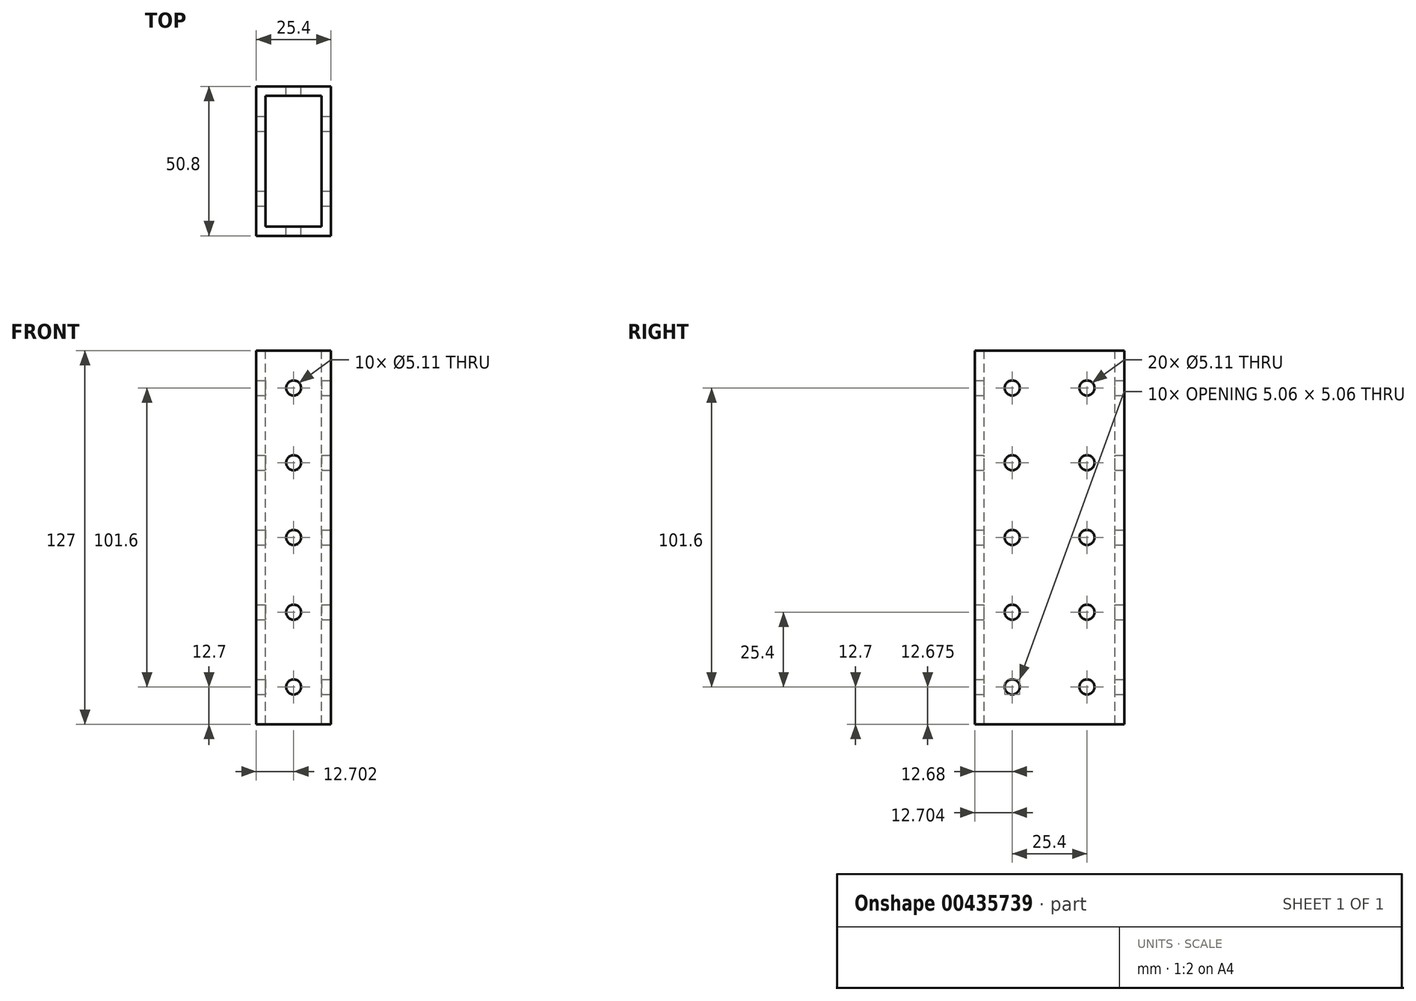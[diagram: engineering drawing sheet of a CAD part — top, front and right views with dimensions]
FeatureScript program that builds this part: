
annotation { "Feature Type Name" : "Feature", "Feature Type Description" : "" }
export const myFeature = defineFeature(function(context is Context, id is Id, definition is map)
    precondition{}
    {
        {
            var Q0;
            Q0=qCreatedBy(makeId("Top.planeOp"),FACE);
            var sketch = newSketch(context, id + "F0", { "sketchPlane" : qUnion([Q0])});
            skLineSegment(sketch, "E0.bottom", {"start": v(-9.87, 8.95) * mm, "end": v(15.53, 8.95) * mm});
            skLineSegment(sketch, "E0.top", {"start": v(-9.87, -41.85) * mm, "end": v(15.53, -41.85) * mm});
            skLineSegment(sketch, "E0.left", {"start": v(-9.87, 8.95) * mm, "end": v(-9.87, -41.85) * mm});
            skLineSegment(sketch, "E0.right", {"start": v(15.53, 8.95) * mm, "end": v(15.53, -41.85) * mm});
            skSolve(sketch);
        }
        {
            var Q0;
            Q0=makeQuery(id+"F0.imprint","IMPRINT",FACE,{"disambiguationData":[TD([[makeQuery(id+"F0.imprint","IMPRINT",EDGE,{"derivedFrom":sQuery(id+"F0.wireOp",EDGE,"E0.bottom")}),-1.0]])]});
            extrude(context, id + "F1", {"entities" : qUnion([Q0]), "depth" : 127 * mm});
        }
        {
            var Q0;
            Q0=makeQuery(id+"F1.opExtrude","CAP_FACE",FACE,{"disambiguationData":[OSD([sQuery(id+"F0.wireOp",EDGE,"E0.bottom"),sQuery(id+"F0.wireOp",EDGE,"E0.top"),sQuery(id+"F0.wireOp",EDGE,"E0.left"),sQuery(id+"F0.wireOp",EDGE,"E0.right")])],"isStart":false});
            var sketch = newSketch(context, id + "F2", { "sketchPlane" : qUnion([Q0])});
            skLineSegment(sketch, "E1.bottom", {"start": v(-6.7, 5.78) * mm, "end": v(12.36, 5.78) * mm});
            skLineSegment(sketch, "E1.top", {"start": v(-6.7, -38.67) * mm, "end": v(12.36, -38.67) * mm});
            skLineSegment(sketch, "E1.left", {"start": v(-6.7, 5.78) * mm, "end": v(-6.7, -38.67) * mm});
            skLineSegment(sketch, "E1.right", {"start": v(12.36, 5.78) * mm, "end": v(12.36, -38.67) * mm});
            skSolve(sketch);
        }
        {
            var Q0;
            Q0=makeQuery(id+"F2.imprint","IMPRINT",FACE,{"disambiguationData":[TD([[makeQuery(id+"F2.imprint","IMPRINT",EDGE,{"derivedFrom":sQuery(id+"F2.wireOp",EDGE,"E1.bottom")}),-1.0]])]});
            extrude(context, id + "F3", {"entities" : qUnion([Q0]), "operationType" : NewBodyOperationType.REMOVE, "oppositeDirection" : true, "depth" : 177.8 * mm});
        }
        {
            var Q0;
            Q0=makeQuery(id+"F1.opExtrude","SWEPT_FACE",FACE,{"disambiguationData":[OSD([sQuery(id+"F0.wireOp",EDGE,"E0.right")])]});
            var sketch = newSketch(context, id + "F4", { "sketchPlane" : qUnion([Q0])});
            skCircle(sketch, "E2", {"center": v(-29.15, 114.3) * mm, "radius": 2.55 * mm});
            skCircle(sketch, "E3.0.1.0", {"center": v(-29.15, 88.9) * mm, "radius": 2.55 * mm});
            skCircle(sketch, "E3.0.2.0", {"center": v(-29.15, 63.5) * mm, "radius": 2.55 * mm});
            skCircle(sketch, "E3.0.3.0", {"center": v(-29.15, 38.1) * mm, "radius": 2.55 * mm});
            skCircle(sketch, "E3.0.4.0", {"center": v(-29.15, 12.7) * mm, "radius": 2.55 * mm});
            skCircle(sketch, "E3.1.0.0", {"center": v(-3.75, 114.3) * mm, "radius": 2.55 * mm});
            skCircle(sketch, "E3.1.1.0", {"center": v(-3.75, 88.9) * mm, "radius": 2.55 * mm});
            skCircle(sketch, "E3.1.2.0", {"center": v(-3.75, 63.5) * mm, "radius": 2.55 * mm});
            skCircle(sketch, "E3.1.3.0", {"center": v(-3.75, 38.1) * mm, "radius": 2.55 * mm});
            skCircle(sketch, "E3.1.4.0", {"center": v(-3.75, 12.7) * mm, "radius": 2.55 * mm});
            skLineSegment(sketch, "E3.direction1", {"start": v(-29.15, 114.3) * mm, "end": v(-3.75, 114.3) * mm, "construction": true});
            skLineSegment(sketch, "E3.direction2", {"start": v(-29.15, 114.3) * mm, "end": v(-29.15, 88.9) * mm, "construction": true});
            skSolve(sketch);
        }
        {
            var Q0;
            Q0=sQuery(id+"F4.wireOp",VERTEX,"E3.1.2.0.center");
            var Q1;
            Q1=sQuery(id+"F4.wireOp",VERTEX,"E3.1.6.0.center");
            var Q2;
            Q2=sQuery(id+"F4.wireOp",VERTEX,"E3.1.3.0.center");
            var Q3;
            Q3=sQuery(id+"F4.wireOp",VERTEX,"E3.1.4.0.center");
            var Q4;
            Q4=sQuery(id+"F4.wireOp",VERTEX,"E2.center");
            var Q5;
            Q5=sQuery(id+"F4.wireOp",VERTEX,"E3.0.1.0.center");
            var Q6;
            Q6=sQuery(id+"F4.wireOp",VERTEX,"E3.0.2.0.center");
            var Q7;
            Q7=sQuery(id+"F4.wireOp",VERTEX,"E3.0.3.0.center");
            var Q8;
            Q8=sQuery(id+"F4.wireOp",VERTEX,"E3.0.4.0.center");
            var Q9;
            Q9=sQuery(id+"F4.wireOp",VERTEX,"E3.0.5.0.center");
            var Q10;
            Q10=sQuery(id+"F4.wireOp",VERTEX,"E3.0.6.0.center");
            var Q11;
            Q11=sQuery(id+"F4.wireOp",VERTEX,"E3.1.0.0.center");
            var Q12;
            Q12=sQuery(id+"F4.wireOp",VERTEX,"E3.1.1.0.center");
            var Q13;
            Q13=sQuery(id+"F4.wireOp",VERTEX,"E3.1.5.0.center");
            var Q14;
            Q14=makeQuery(id+"F1.opExtrude","SWEPT_BODY",BODY,{"disambiguationData":[OSD([sQuery(id+"F0.wireOp",EDGE,"E0.bottom"),sQuery(id+"F0.wireOp",EDGE,"E0.top"),sQuery(id+"F0.wireOp",EDGE,"E0.left"),sQuery(id+"F0.wireOp",EDGE,"E0.right")])]});
            hole(context, id + "F5", {"style" : HoleStyle.SIMPLE, "endStyle" : HoleEndStyle.THROUGH, "holeDiameter" : 5.1 * mm, "isTappedThrough" : true, "tappedDepth" : 12.7 * mm, "tapClearance" : 3, "locations" : qUnion([Q0, Q1, Q2, Q3, Q4, Q5, Q6, Q7, Q8, Q9, Q10, Q11, Q12, Q13]), "scope" : qUnion([Q14])});
        }
        {
            var Q0;
            Q0=makeQuery(id+"F1.opExtrude","SWEPT_FACE",FACE,{"disambiguationData":[OSD([sQuery(id+"F0.wireOp",EDGE,"E0.bottom")])]});
            var sketch = newSketch(context, id + "F6", { "sketchPlane" : qUnion([Q0])});
            skCircle(sketch, "E4", {"center": v(-2.83, 114.3) * mm, "radius": 2.55 * mm});
            skCircle(sketch, "E5.0.1.0", {"center": v(-2.83, 88.9) * mm, "radius": 2.55 * mm});
            skCircle(sketch, "E5.0.2.0", {"center": v(-2.83, 63.5) * mm, "radius": 2.55 * mm});
            skCircle(sketch, "E5.0.3.0", {"center": v(-2.83, 38.1) * mm, "radius": 2.55 * mm});
            skCircle(sketch, "E5.0.4.0", {"center": v(-2.83, 12.7) * mm, "radius": 2.55 * mm});
            skLineSegment(sketch, "E5.direction1", {"start": v(-2.83, 114.3) * mm, "end": v(22.57, 114.3) * mm, "construction": true});
            skLineSegment(sketch, "E5.direction2", {"start": v(-2.83, 114.3) * mm, "end": v(-2.83, 88.9) * mm, "construction": true});
            skSolve(sketch);
        }
        {
            var Q0;
            Q0=sQuery(id+"F6.wireOp",VERTEX,"E5.0.1.0.center");
            var Q1;
            Q1=sQuery(id+"F6.wireOp",VERTEX,"E5.direction1.start");
            var Q2;
            Q2=sQuery(id+"F6.wireOp",VERTEX,"E5.0.2.0.center");
            var Q3;
            Q3=sQuery(id+"F6.wireOp",VERTEX,"E5.0.3.0.center");
            var Q4;
            Q4=sQuery(id+"F6.wireOp",VERTEX,"E5.0.5.0.center");
            var Q5;
            Q5=sQuery(id+"F6.wireOp",VERTEX,"E5.0.4.0.center");
            var Q6;
            Q6=sQuery(id+"F6.wireOp",VERTEX,"E5.0.6.0.center");
            var Q7;
            Q7=makeQuery(id+"F1.opExtrude","SWEPT_BODY",BODY,{"disambiguationData":[OSD([sQuery(id+"F0.wireOp",EDGE,"E0.bottom"),sQuery(id+"F0.wireOp",EDGE,"E0.top"),sQuery(id+"F0.wireOp",EDGE,"E0.left"),sQuery(id+"F0.wireOp",EDGE,"E0.right")])]});
            hole(context, id + "F7", {"style" : HoleStyle.SIMPLE, "endStyle" : HoleEndStyle.THROUGH, "holeDiameter" : 5.1 * mm, "isTappedThrough" : true, "tappedDepth" : 12.7 * mm, "tapClearance" : 3, "locations" : qUnion([Q0, Q1, Q2, Q3, Q4, Q5, Q6]), "scope" : qUnion([Q7])});
        }
    });
